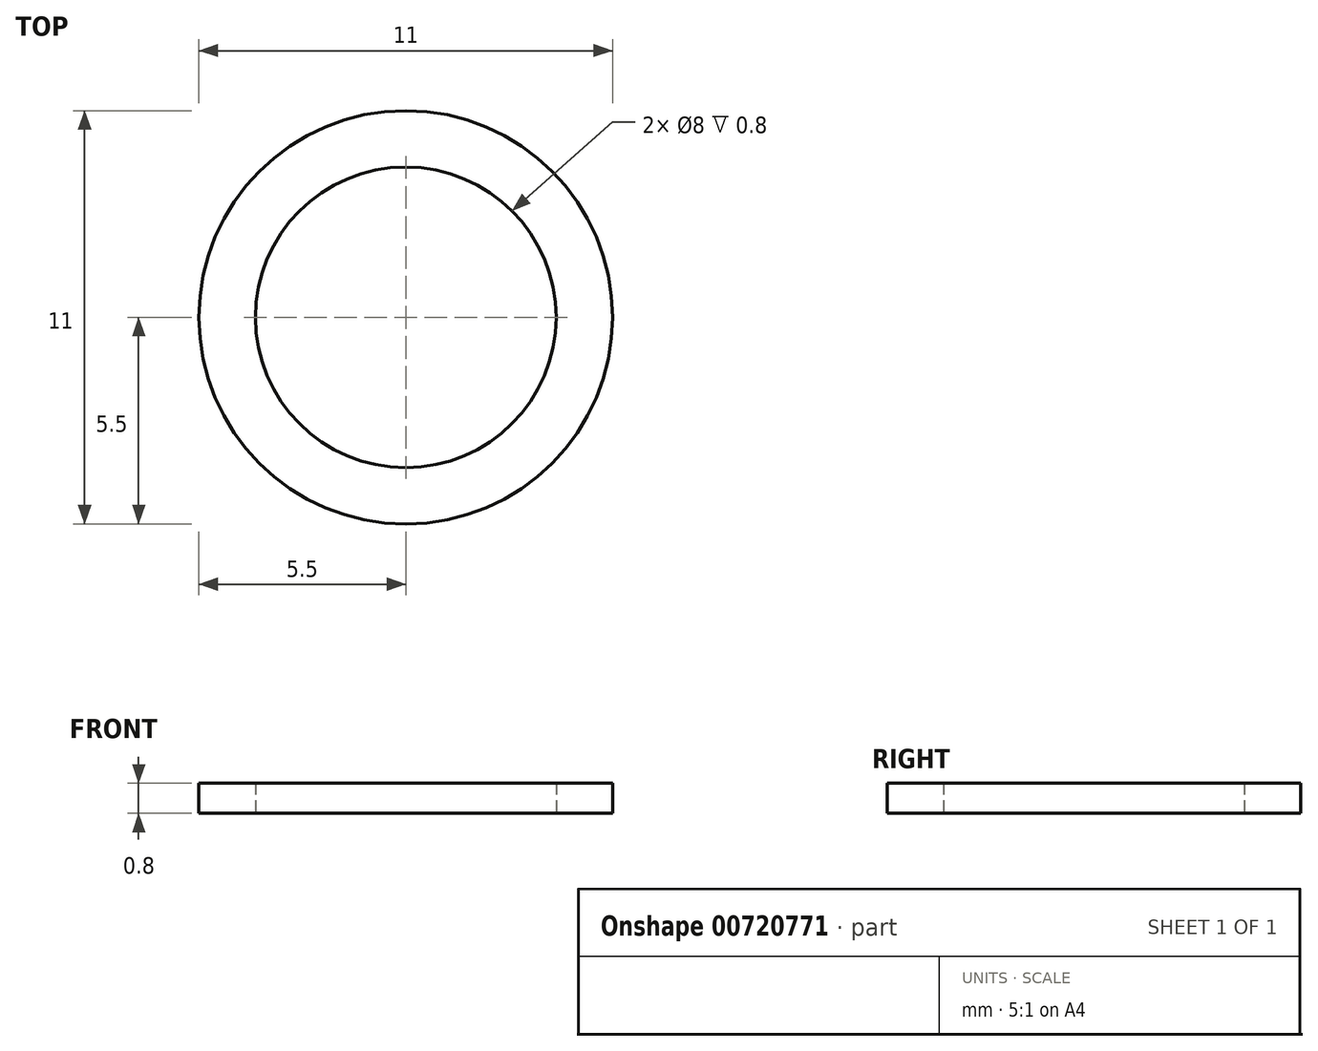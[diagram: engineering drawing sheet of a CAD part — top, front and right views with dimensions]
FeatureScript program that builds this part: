
annotation { "Feature Type Name" : "Feature", "Feature Type Description" : "" }
export const myFeature = defineFeature(function(context is Context, id is Id, definition is map)
    precondition{}
    {
        {
            var Q0;
            Q0=qCreatedBy(makeId("Top.planeOp"),FACE);
            var sketch = newSketch(context, id + "F0", { "sketchPlane" : qUnion([Q0])});
            skCircle(sketch, "E0", {"center": v(0, 0) * mm, "radius": 4 * mm});
            skCircle(sketch, "E1", {"center": v(0, 0) * mm, "radius": 5.5 * mm});
            skSolve(sketch);
        }
        {
            var Q0;
            Q0 = qSketchRegion(id + "F0", true);
            extrude(context, id + "F1", {"entities" : qUnion([Q0]), "depth" : .8 * mm, "offsetDistance" : 25 * mm});
        }
    });
